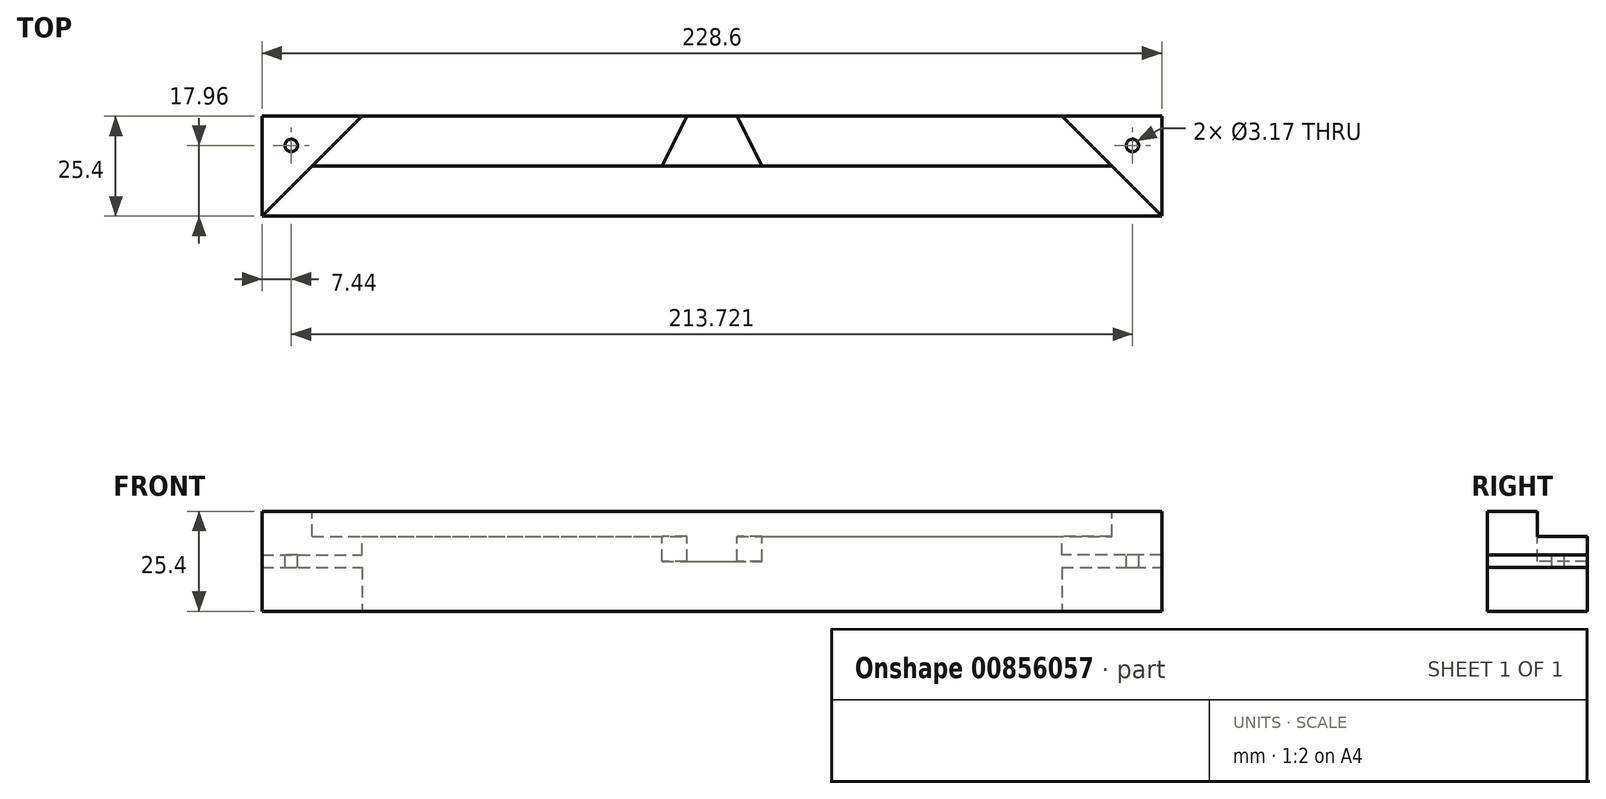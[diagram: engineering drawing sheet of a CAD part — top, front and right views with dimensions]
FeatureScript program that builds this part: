
annotation { "Feature Type Name" : "Feature", "Feature Type Description" : "" }
export const myFeature = defineFeature(function(context is Context, id is Id, definition is map)
    precondition{}
    {
        {
            var Q0;
            Q0=qCreatedBy(makeId("Front.planeOp"),FACE);
            var sketch = newSketch(context, id + "F0", { "sketchPlane" : qUnion([Q0])});
            skLineSegment(sketch, "E0.bottom", {"start": v(-119.16, 17.53) * mm, "end": v(109.44, 17.53) * mm});
            skLineSegment(sketch, "E0.top", {"start": v(-119.16, -7.87) * mm, "end": v(109.44, -7.87) * mm});
            skLineSegment(sketch, "E0.left", {"start": v(-119.16, 17.53) * mm, "end": v(-119.16, -7.87) * mm});
            skLineSegment(sketch, "E0.right", {"start": v(109.44, 17.53) * mm, "end": v(109.44, -7.87) * mm});
            skSolve(sketch);
        }
        {
            var Q0;
            Q0=makeQuery(id+"F0.imprint","IMPRINT",FACE,{"disambiguationData":[TD([[makeQuery(id+"F0.imprint","IMPRINT",EDGE,{"derivedFrom":sQuery(id+"F0.wireOp",EDGE,"E0.bottom")}),-1.0]])]});
            extrude(context, id + "F1", {"entities" : qUnion([Q0]), "depth" : 25.4 * mm, "offsetDistance" : 25.4 * mm});
        }
        {
            var Q0;
            Q0=makeQuery(id+"F1.opExtrude","SWEPT_FACE",FACE,{"disambiguationData":[OSD([sQuery(id+"F0.wireOp",EDGE,"E0.bottom")])]});
            var sketch = newSketch(context, id + "F2", { "sketchPlane" : qUnion([Q0])});
            skLineSegment(sketch, "E1", {"start": v(-119.16, -25.4) * mm, "end": v(-93.76, 0) * mm});
            skLineSegment(sketch, "E2", {"start": v(109.44, -25.4) * mm, "end": v(84.04, 0) * mm});
            skLineSegment(sketch, "E3", {"start": v(-106.46, -12.7) * mm, "end": v(96.74, -12.7) * mm});
            skSolve(sketch);
        }
        {
            var Q0;
            {var subQ0=sQuery(id+"F2.wireOp",EDGE,"E1");Q0=makeQuery(id+"F2.imprint","IMPRINT",FACE,{"disambiguationData":[TD([[makeQuery(id+"F2.imprint","IMPRINT",EDGE,{"derivedFrom":subQ0}),1.0]])]});}
            var Q1;
            {var subQ0=sQuery(id+"F2.wireOp",EDGE,"E2");Q1=makeQuery(id+"F2.imprint","IMPRINT",FACE,{"disambiguationData":[TD([[makeQuery(id+"F2.imprint","IMPRINT",EDGE,{"derivedFrom":subQ0}),-1.0]])]});}
            extrude(context, id + "F3", {"entities" : qUnion([Q0, Q1]), "operationType" : NewBodyOperationType.REMOVE, "oppositeDirection" : true, "depth" : 11.1 * mm, "offsetDistance" : 25.4 * mm});
        }
        {
            var Q0;
            Q0=makeQuery(id+"F1.opExtrude","SWEPT_FACE",FACE,{"disambiguationData":[OSD([sQuery(id+"F0.wireOp",EDGE,"E0.top")])]});
            var sketch = newSketch(context, id + "F4", { "sketchPlane" : qUnion([Q0])});
            skLineSegment(sketch, "E4", {"start": v(-119.16, 25.4) * mm, "end": v(-93.76, 0) * mm});
            skLineSegment(sketch, "E5", {"start": v(109.44, 25.4) * mm, "end": v(84.04, 0) * mm});
            skSolve(sketch);
        }
        {
            var Q0;
            {var subQ0=sQuery(id+"F4.wireOp",EDGE,"E4");Q0=makeQuery(id+"F4.imprint","IMPRINT",FACE,{"disambiguationData":[TD([[makeQuery(id+"F4.imprint","IMPRINT",EDGE,{"derivedFrom":subQ0}),-1.0]])]});}
            var Q1;
            {var subQ0=sQuery(id+"F4.wireOp",EDGE,"E5");Q1=makeQuery(id+"F4.imprint","IMPRINT",FACE,{"disambiguationData":[TD([[makeQuery(id+"F4.imprint","IMPRINT",EDGE,{"derivedFrom":subQ0}),1.0]])]});}
            extrude(context, id + "F5", {"entities" : qUnion([Q0, Q1]), "operationType" : NewBodyOperationType.REMOVE, "oppositeDirection" : true, "depth" : 11.1 * mm, "offsetDistance" : 25.4 * mm});
        }
        {
            var Q0;
            {var subQ3=sQuery(id+"F2.wireOp",EDGE,"E3");Q0=makeQuery(id+"F2.imprint","IMPRINT",FACE,{"disambiguationData":[TD([[makeQuery(id+"F2.imprint","IMPRINT",EDGE,{"derivedFrom":subQ3}),1.0]])]});}
            extrude(context, id + "F6", {"entities" : qUnion([Q0]), "operationType" : NewBodyOperationType.REMOVE, "oppositeDirection" : true, "depth" : 6.35 * mm, "offsetDistance" : 25.4 * mm});
        }
        {
            var Q0;
            Q0=makeQuery(id+"F6.boolean.opBoolean","COPY",FACE,{"derivedFrom":makeQuery(id+"F6.opExtrude","CAP_FACE",FACE,{"disambiguationData":[OSD([sQuery(id+"F0.wireOp",EDGE,"E0.bottom"),sQuery(id+"F2.wireOp",EDGE,"E1"),sQuery(id+"F2.wireOp",EDGE,"E2"),sQuery(id+"F2.wireOp",EDGE,"E3")])],"isStart":false})});
            var sketch = newSketch(context, id + "F7", { "sketchPlane" : qUnion([Q0])});
            skLineSegment(sketch, "E6", {"start": v(-11.2, 0) * mm, "end": v(-17.56, -12.7) * mm});
            skLineSegment(sketch, "E7", {"start": v(-17.56, -12.7) * mm, "end": v(7.84, -12.7) * mm});
            skLineSegment(sketch, "E8", {"start": v(7.84, -12.7) * mm, "end": v(1.5, 0) * mm});
            skLineSegment(sketch, "E9", {"start": v(-106.46, -12.7) * mm, "end": v(-17.56, -12.7) * mm});
            skLineSegment(sketch, "E10", {"start": v(7.84, -12.7) * mm, "end": v(96.74, -12.7) * mm});
            skSolve(sketch);
        }
        {
            var Q0;
            {var subQ0=sQuery(id+"F7.wireOp",EDGE,"E6");Q0=makeQuery(id+"F7.imprint","IMPRINT",FACE,{"disambiguationData":[TD([[makeQuery(id+"F7.imprint","IMPRINT",EDGE,{"derivedFrom":subQ0}),1.0]])]});}
            extrude(context, id + "F8", {"entities" : qUnion([Q0]), "operationType" : NewBodyOperationType.REMOVE, "oppositeDirection" : true, "depth" : 6.35 * mm, "offsetDistance" : 25.4 * mm});
        }
        {
            var Q0;
            Q0=makeQuery(id+"F3.boolean.opBoolean","COPY",FACE,{"derivedFrom":makeQuery(id+"F3.opExtrude","CAP_FACE",FACE,{"disambiguationData":[OSD([sQuery(id+"F0.wireOp",EDGE,"E0.bottom"),sQuery(id+"F0.wireOp",EDGE,"E0.left"),sQuery(id+"F2.wireOp",EDGE,"E1")])],"isStart":false})});
            var sketch = newSketch(context, id + "F9", { "sketchPlane" : qUnion([Q0])});
            skCircle(sketch, "E11", {"center": v(-111.72, -7.44) * mm, "radius": 1.59 * mm});
            skLineSegment(sketch, "E12", {"start": v(-111.72, -7.44) * mm, "end": v(-119.16, -7.44) * mm});
            skLineSegment(sketch, "E13", {"start": v(-111.72, -7.44) * mm, "end": v(-111.72, 0) * mm});
            skLineSegment(sketch, "E14", {"start": v(-111.72, -7.44) * mm, "end": v(-106.46, -12.7) * mm});
            skSolve(sketch);
        }
        {
            var Q0;
            Q0=makeQuery(id+"F3.boolean.opBoolean","COPY",FACE,{"derivedFrom":makeQuery(id+"F3.opExtrude","CAP_FACE",FACE,{"disambiguationData":[OSD([sQuery(id+"F0.wireOp",EDGE,"E0.bottom"),sQuery(id+"F0.wireOp",EDGE,"E0.right"),sQuery(id+"F2.wireOp",EDGE,"E2")])],"isStart":false})});
            var sketch = newSketch(context, id + "F10", { "sketchPlane" : qUnion([Q0])});
            skCircle(sketch, "E15", {"center": v(102, -7.44) * mm, "radius": 1.59 * mm});
            skLineSegment(sketch, "E16", {"start": v(102, -7.44) * mm, "end": v(102, 0) * mm});
            skLineSegment(sketch, "E17", {"start": v(102, -7.44) * mm, "end": v(109.44, -7.44) * mm});
            skPoint(sketch, "E18.endSnap0", {"position": v(96.74, -12.7) * mm});
            skLineSegment(sketch, "E19", {"start": v(102, -7.44) * mm, "end": v(96.74, -12.7) * mm});
            skSolve(sketch);
        }
        {
            var Q0;
            {var subQ0=sQuery(id+"F9.wireOp",EDGE,"E13");var subQ1=sQuery(id+"F9.wireOp",EDGE,"E11");var subQ2=makeQuery(id+"F9.imprint","INTERSECT",VERTEX,{"derivedFrom":[subQ1,subQ0]});Q0=makeQuery(id+"F9.imprint","IMPRINT",FACE,{"disambiguationData":[TD([[makeQuery(id+"F9.imprint","IMPRINT",EDGE,{"disambiguationData":[TD([[subQ2,1.0]])],"derivedFrom":subQ1}),1.0]])]});}
            var Q1;
            {var subQ0=sQuery(id+"F9.wireOp",EDGE,"E12");var subQ1=sQuery(id+"F9.wireOp",EDGE,"E11");var subQ2=makeQuery(id+"F9.imprint","INTERSECT",VERTEX,{"derivedFrom":[subQ1,subQ0]});Q1=makeQuery(id+"F9.imprint","IMPRINT",FACE,{"disambiguationData":[TD([[makeQuery(id+"F9.imprint","IMPRINT",EDGE,{"disambiguationData":[TD([[subQ2,1.0]])],"derivedFrom":subQ1}),1.0]])]});}
            var Q2;
            {var subQ0=sQuery(id+"F9.wireOp",EDGE,"E12");var subQ1=sQuery(id+"F9.wireOp",EDGE,"E11");var subQ2=makeQuery(id+"F9.imprint","INTERSECT",VERTEX,{"derivedFrom":[subQ1,subQ0]});Q2=makeQuery(id+"F9.imprint","IMPRINT",FACE,{"disambiguationData":[TD([[makeQuery(id+"F9.imprint","IMPRINT",EDGE,{"disambiguationData":[TD([[subQ2,-1.0]])],"derivedFrom":subQ1}),1.0]])]});}
            var Q3;
            {var subQ0=sQuery(id+"F10.wireOp",EDGE,"E16");var subQ1=sQuery(id+"F10.wireOp",EDGE,"E15");var subQ2=makeQuery(id+"F10.imprint","INTERSECT",VERTEX,{"derivedFrom":[subQ1,subQ0]});Q3=makeQuery(id+"F10.imprint","IMPRINT",FACE,{"disambiguationData":[TD([[makeQuery(id+"F10.imprint","IMPRINT",EDGE,{"disambiguationData":[TD([[subQ2,1.0]])],"derivedFrom":subQ1}),1.0]])]});}
            var Q4;
            {var subQ0=sQuery(id+"F10.wireOp",EDGE,"E16");var subQ1=sQuery(id+"F10.wireOp",EDGE,"E15");var subQ2=makeQuery(id+"F10.imprint","INTERSECT",VERTEX,{"derivedFrom":[subQ1,subQ0]});Q4=makeQuery(id+"F10.imprint","IMPRINT",FACE,{"disambiguationData":[TD([[makeQuery(id+"F10.imprint","IMPRINT",EDGE,{"disambiguationData":[TD([[subQ2,-1.0]])],"derivedFrom":subQ1}),1.0]])]});}
            var Q5;
            {var subQ0=sQuery(id+"F10.wireOp",EDGE,"E17");var subQ1=sQuery(id+"F10.wireOp",EDGE,"E15");var subQ2=makeQuery(id+"F10.imprint","INTERSECT",VERTEX,{"derivedFrom":[subQ1,subQ0]});Q5=makeQuery(id+"F10.imprint","IMPRINT",FACE,{"disambiguationData":[TD([[makeQuery(id+"F10.imprint","IMPRINT",EDGE,{"disambiguationData":[TD([[subQ2,1.0]])],"derivedFrom":subQ1}),1.0]])]});}
            extrude(context, id + "F11", {"entities" : qUnion([Q0, Q1, Q2, Q3, Q4, Q5]), "operationType" : NewBodyOperationType.REMOVE, "oppositeDirection" : true, "depth" : 25.4 * mm, "offsetDistance" : 25.4 * mm});
        }
    });
